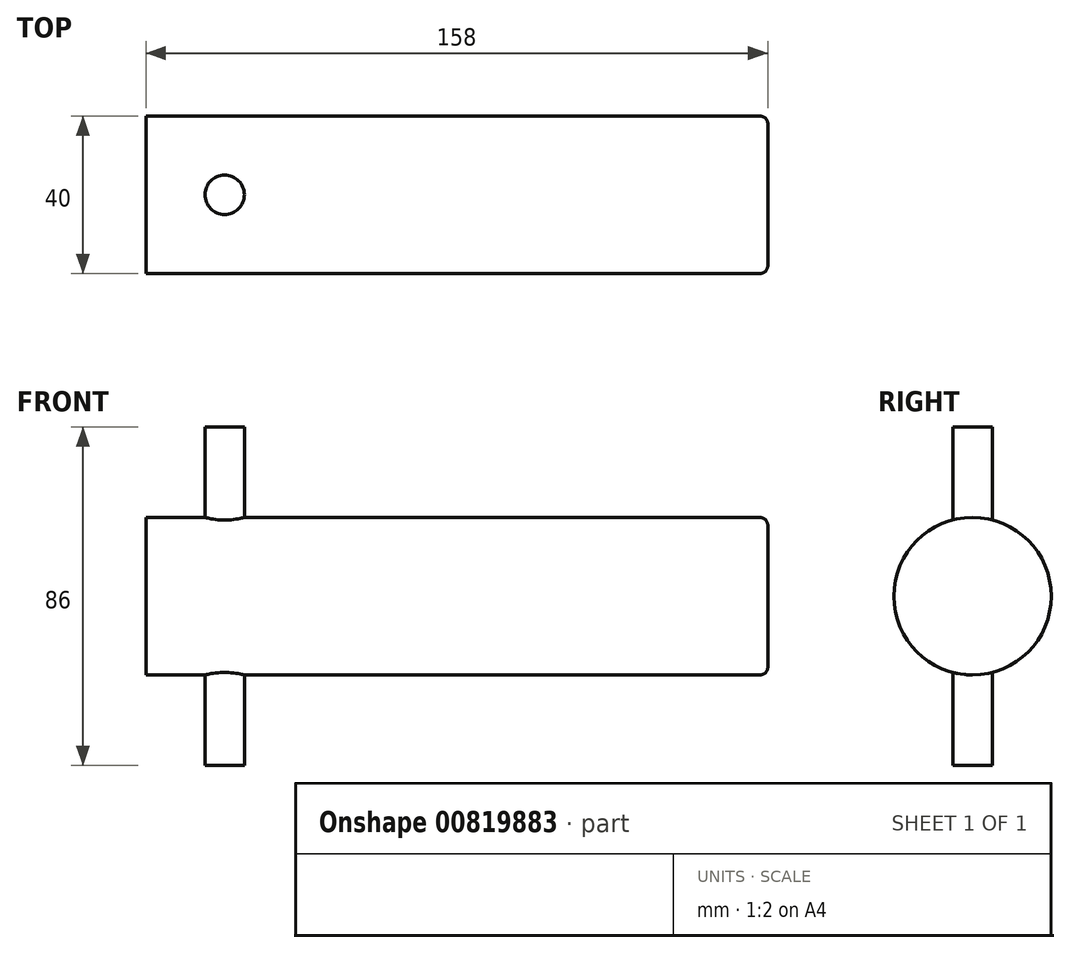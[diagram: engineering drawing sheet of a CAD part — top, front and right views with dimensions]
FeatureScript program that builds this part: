
annotation { "Feature Type Name" : "Feature", "Feature Type Description" : "" }
export const myFeature = defineFeature(function(context is Context, id is Id, definition is map)
    precondition{}
    {
        {
            var Q0;
            Q0=qCreatedBy(makeId("Right.planeOp"),FACE);
            var sketch = newSketch(context, id + "F0", { "sketchPlane" : qUnion([Q0])});
            skCircle(sketch, "E0", {"center": v(0, 0) * mm, "radius": 20 * mm});
            skSolve(sketch);
        }
        {
            var Q0;
            Q0 = qSketchRegion(id + "F0", true);
            extrude(context, id + "F1", {"entities" : qUnion([Q0]), "depth" : 158 * mm, "offsetDistance" : 25 * mm});
        }
        {
            var Q0;
            Q0=qCreatedBy(makeId("Top.planeOp"),FACE);
            var sketch = newSketch(context, id + "F2", { "sketchPlane" : qUnion([Q0])});
            skCircle(sketch, "E1", {"center": v(20, 0) * mm, "radius": 5 * mm});
            skSolve(sketch);
        }
        {
            var Q0;
            Q0 = qSketchRegion(id + "F2", true);
            extrude(context, id + "F3", {"entities" : qUnion([Q0]), "operationType" : NewBodyOperationType.ADD, "endBound" : BoundingType.SYMMETRIC, "depth" : 86 * mm, "offsetDistance" : 25 * mm});
        }
        {
            var Q0;
            Q0=makeQuery(id+"F1.opExtrude","CAP_EDGE",EDGE,{"disambiguationData":[OSD([sQuery(id+"F0.wireOp",EDGE,"E0")])],"isStart":false});
            fillet(context, id + "F4", {"entities" : qUnion([Q0]), "radius" : 2 * mm, "tangentPropagation" : true, "allowEdgeOverflow" : false});
        }
    });
